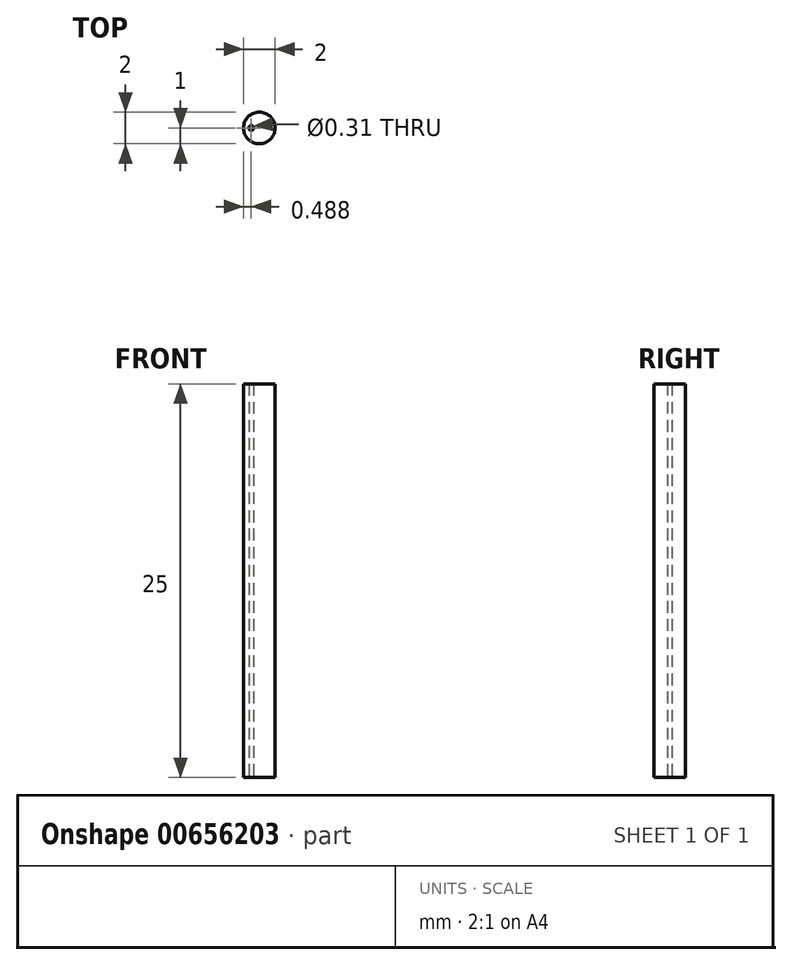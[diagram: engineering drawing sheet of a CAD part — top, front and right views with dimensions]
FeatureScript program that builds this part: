
annotation { "Feature Type Name" : "Feature", "Feature Type Description" : "" }
export const myFeature = defineFeature(function(context is Context, id is Id, definition is map)
    precondition{}
    {
        {
            var Q0;
            Q0=qCreatedBy(makeId("Top.planeOp"),FACE);
            var sketch = newSketch(context, id + "F0", { "sketchPlane" : qUnion([Q0])});
            skCircle(sketch, "E0", {"center": v(0, 0) * mm, "radius": 1 * mm});
            skCircle(sketch, "E1", {"center": v(-0.51, 0) * mm, "radius": 0.15 * mm});
            skSolve(sketch);
        }
        {
            var Q0;
            Q0=makeQuery(id+"F0.imprint","IMPRINT",FACE,{"disambiguationData":[TD([[makeQuery(id+"F0.imprint","IMPRINT",EDGE,{"derivedFrom":sQuery(id+"F0.wireOp",EDGE,"E0")}),1.0]])]});
            extrude(context, id + "F1", {"entities" : qUnion([Q0]), "depth" : 25 * mm, "offsetDistance" : 25 * mm});
        }
    });
